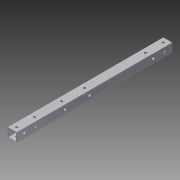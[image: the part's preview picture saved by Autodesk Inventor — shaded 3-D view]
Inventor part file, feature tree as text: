
AUTODESK INVENTOR PART (.ipt)
format: ipt  version: 2014 SP1 (Build 180222100, 222)  size: 115,200 bytes
history: native  units: in
note: dims shown in document units (in); Inventor stores cm internally (conversion verified against a paired STEP export)
features: reference x11, extrude x3, sketch x3
ambient origin geometry x8: Origin, YZ Plane, XZ Plane, XY Plane, X Axis, Y Axis, Z Axis, Center Point
bodies: Solid1 (feature_tree)
feature tree (17):
  extrude  "Extrusion1"  Depth=1.0in
  extrude  "Extrusion2"  Depth=17.5in TaperAngle=0.0deg
  extrude  "Extrusion3"  Depth=1.0in TaperAngle=0.0deg
  sketch  "Sketch1"  dims[d0=1.0in d1=1.0in]
  sketch  "Sketch2"  dims[d2=0.0625in d3=17.5in d4=0.0in]
  sketch  "Sketch3"  dims[d5=1.0in d6=0.0in d7=1.0in d8=0.0in]
  reference  "Reference7"
  reference  "Reference8"
  reference  "Reference9"
  reference  "Reference10"
  reference  "Reference11"
  reference  "Reference12"
  reference  "Reference13"
  reference  "Reference14"
  reference  "Reference15"
  reference  "Reference16"
  reference  "Reference17"
